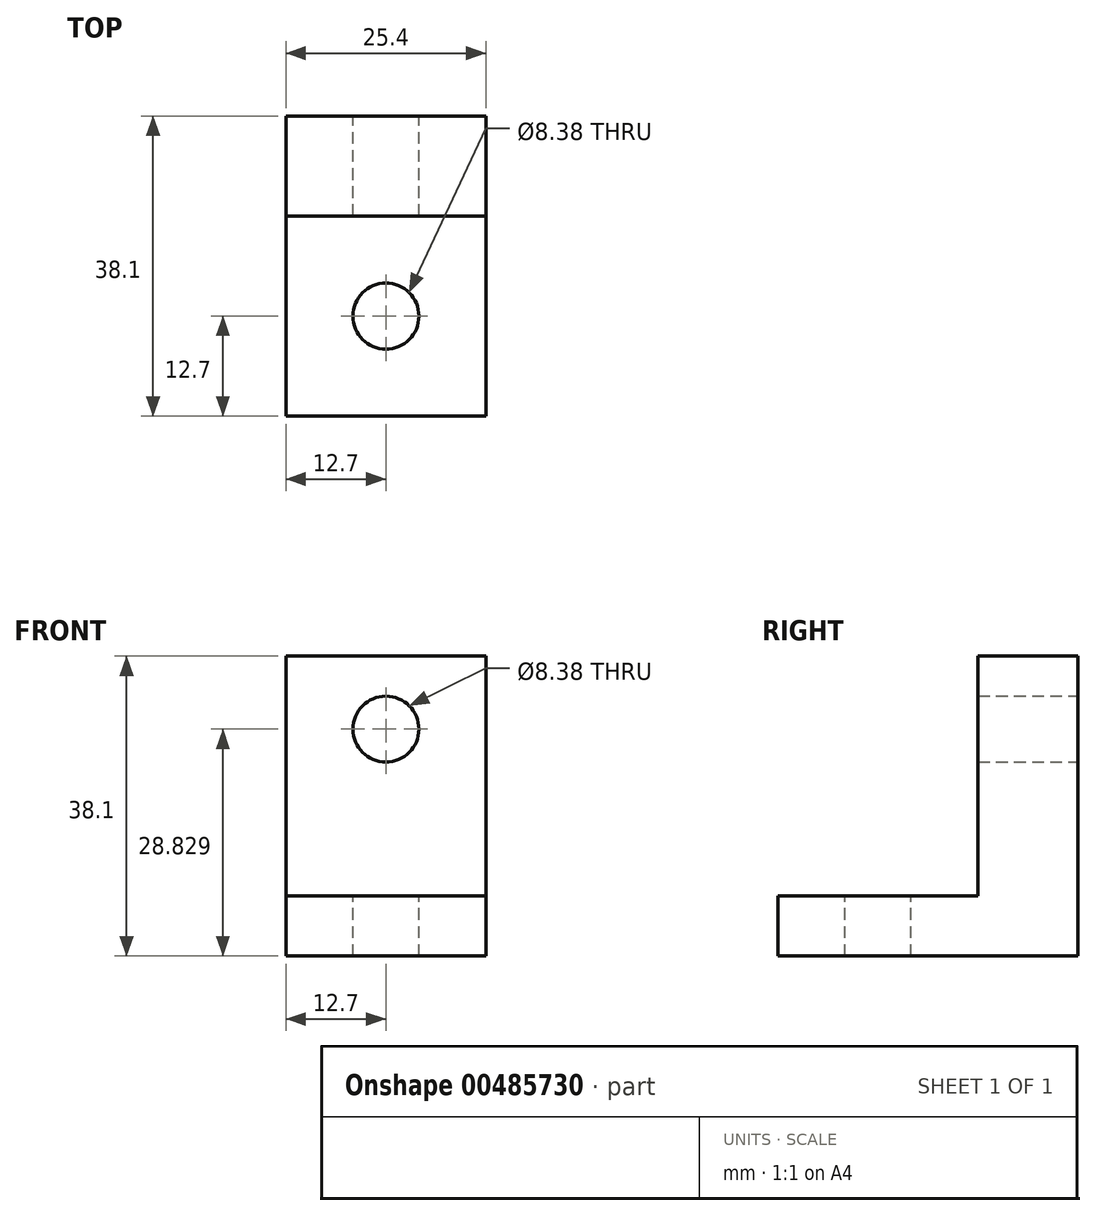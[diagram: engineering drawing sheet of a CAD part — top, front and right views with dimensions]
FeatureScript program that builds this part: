
annotation { "Feature Type Name" : "Feature", "Feature Type Description" : "" }
export const myFeature = defineFeature(function(context is Context, id is Id, definition is map)
    precondition{}
    {
        {
            var Q0;
            Q0=qCreatedBy(makeId("Front.planeOp"),FACE);
            var sketch = newSketch(context, id + "F0", { "sketchPlane" : qUnion([Q0])});
            skLineSegment(sketch, "E0.bottom", {"start": v(12.7, 19.05) * mm, "end": v(-12.7, 19.05) * mm});
            skLineSegment(sketch, "E0.top", {"start": v(12.7, -19.05) * mm, "end": v(-12.7, -19.05) * mm});
            skLineSegment(sketch, "E0.left", {"start": v(12.7, 19.05) * mm, "end": v(12.7, -19.05) * mm});
            skLineSegment(sketch, "E0.right", {"start": v(-12.7, 19.05) * mm, "end": v(-12.7, -19.05) * mm});
            skPoint(sketch, "E0.middle", {"position": v(0, 0) * mm});
            skCircle(sketch, "E1", {"center": v(0, 9.78) * mm, "radius": 4.2 * mm});
            skLineSegment(sketch, "E2", {"start": v(-12.7, -11.43) * mm, "end": v(12.7, -11.43) * mm});
            skSolve(sketch);
        }
        {
            var Q0;
            {var subQ1=sQuery(id+"F0.wireOp",EDGE,"E0.bottom");Q0=makeQuery(id+"F0.imprint","IMPRINT",FACE,{"disambiguationData":[TD([[makeQuery(id+"F0.imprint","IMPRINT",EDGE,{"derivedFrom":subQ1}),1.0]])]});}
            extrude(context, id + "F1", {"entities" : qUnion([Q0]), "depth" : 12.7 * mm});
        }
        {
            var Q0;
            {var subQ0=sQuery(id+"F0.wireOp",EDGE,"E0.top");Q0=makeQuery(id+"F0.imprint","IMPRINT",FACE,{"disambiguationData":[TD([[makeQuery(id+"F0.imprint","IMPRINT",EDGE,{"derivedFrom":subQ0}),-1.0]])]});}
            extrude(context, id + "F2", {"entities" : qUnion([Q0]), "operationType" : NewBodyOperationType.ADD, "depth" : 38.1 * mm});
        }
        {
            var Q0;
            Q0=makeQuery(id+"F2.opExtrude","SWEPT_FACE",FACE,{"disambiguationData":[OSD([sQuery(id+"F0.wireOp",EDGE,"E2")])]});
            var sketch = newSketch(context, id + "F3", { "sketchPlane" : qUnion([Q0])});
            skPoint(sketch, "E3", {"position": v(0, -25.4) * mm});
            skSolve(sketch);
        }
        {
            var Q0;
            Q0=sQuery(id+"F3.wireOp",VERTEX,"E3");
            var Q1;
            Q1=makeQuery(id+"F1.opExtrude","SWEPT_BODY",BODY,{"disambiguationData":[OSD([sQuery(id+"F0.wireOp",EDGE,"E0.bottom"),sQuery(id+"F0.wireOp",EDGE,"E0.left"),sQuery(id+"F0.wireOp",EDGE,"E0.right"),sQuery(id+"F0.wireOp",EDGE,"E1"),sQuery(id+"F0.wireOp",EDGE,"E2")])]});
            hole(context, id + "F4", {"style" : HoleStyle.SIMPLE, "endStyle" : HoleEndStyle.BLIND, "holeDiameter" : 8.38 * mm, "holeDepth" : 12.7 * mm, "isTappedThrough" : true, "tappedDepth" : 12.7 * mm, "tapClearance" : 3, "locations" : qUnion([Q0]), "scope" : qUnion([Q1])});
        }
    });
